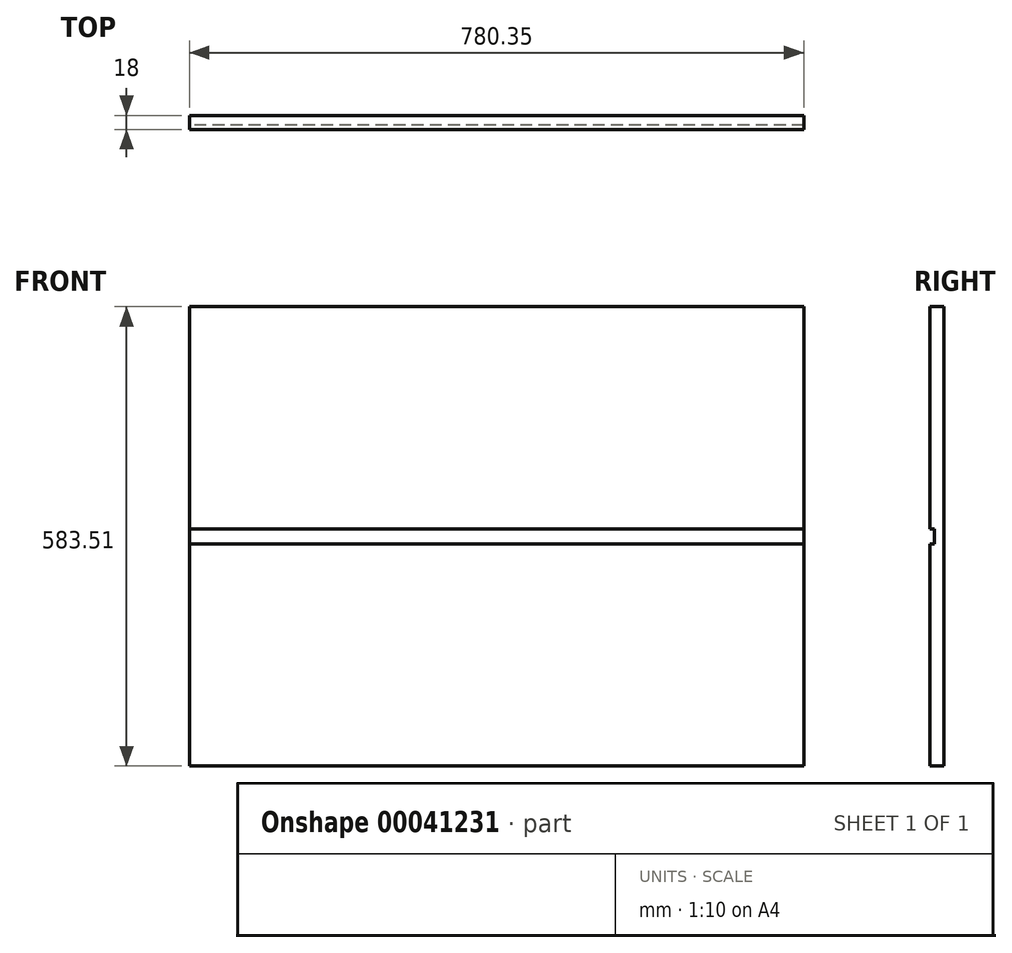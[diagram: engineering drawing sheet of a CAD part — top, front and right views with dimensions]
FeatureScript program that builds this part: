
annotation { "Feature Type Name" : "Feature", "Feature Type Description" : "" }
export const myFeature = defineFeature(function(context is Context, id is Id, definition is map)
    precondition{}
    {
        {
            var Q0;
            Q0=qCreatedBy(makeId("Front.planeOp"),FACE);
            var sketch = newSketch(context, id + "F0", { "sketchPlane" : qUnion([Q0])});
            skLineSegment(sketch, "E0.bottom", {"start": v(-384.92, 365.69) * mm, "end": v(395.43, 365.69) * mm});
            skLineSegment(sketch, "E0.top", {"start": v(-384.92, -217.82) * mm, "end": v(395.43, -217.82) * mm});
            skLineSegment(sketch, "E0.left", {"start": v(-384.92, 365.69) * mm, "end": v(-384.92, -217.82) * mm});
            skLineSegment(sketch, "E0.right", {"start": v(395.43, 365.69) * mm, "end": v(395.43, -217.82) * mm});
            skSolve(sketch);
        }
        {
            var Q0;
            Q0 = qSketchRegion(id + "F0", true);
            extrude(context, id + "F1", {"entities" : qUnion([Q0]), "depth" : 18 * mm});
        }
        {
            var Q0;
            Q0=makeQuery(id+"F1.opExtrude","CAP_FACE",FACE,{"disambiguationData":[OSD([sQuery(id+"F0.wireOp",EDGE,"E0.bottom"),sQuery(id+"F0.wireOp",EDGE,"E0.top"),sQuery(id+"F0.wireOp",EDGE,"E0.left"),sQuery(id+"F0.wireOp",EDGE,"E0.right")])],"isStart":false});
            var sketch = newSketch(context, id + "F2", { "sketchPlane" : qUnion([Q0])});
            skLineSegment(sketch, "E1", {"start": v(395.43, 73.94) * mm, "end": v(-384.92, 73.94) * mm, "construction": true});
            skLineSegment(sketch, "E2.bottom", {"start": v(416.84, 64.44) * mm, "end": v(-399.54, 64.44) * mm});
            skLineSegment(sketch, "E2.top", {"start": v(416.84, 83.44) * mm, "end": v(-399.54, 83.44) * mm});
            skLineSegment(sketch, "E2.left", {"start": v(416.84, 64.44) * mm, "end": v(416.84, 83.44) * mm});
            skLineSegment(sketch, "E2.right", {"start": v(-399.54, 64.44) * mm, "end": v(-399.54, 83.44) * mm});
            skSolve(sketch);
        }
        {
            var Q0;
            Q0 = qSketchRegion(id + "F2", true);
            extrude(context, id + "F3", {"entities" : qUnion([Q0]), "operationType" : NewBodyOperationType.REMOVE, "oppositeDirection" : true, "depth" : 6 * mm});
        }
    });
